# Revit family: Shower-Shower_Door-KOHLER-Prim-K-706533.rfa_
name_source: partatom
category: Specialty Equipment
units: mm (PartAtom-declared; Revit-internal decimal feet)

## family parameters
Cut with Voids When Loaded = No
Host = Face
OmniClass Number = 23.31.17.17
OmniClass Title = Shower Enclosures
Part Type = Normal
Room Calculation Point = No
Round Connector Dimension = Use Diameter
Shared = No

## types (6) — shared parameters
ADA Compliant = No
Assembly Code = C1030200
Date Modified = 06/28/2023
Default Elevation = 4"
Height = 79 1/16"
Length = 5 9/16"
Manufacturer = Kohler Co.
Master Format 2014 = 10 28 19.16
Master Format 2014 Name = Shower Doors
Material = Premium Metal Construction
Product Documentation Link = https://www.us.kohler.com
Product Name = Prim
Product Page URL = http://www.us.kohler.com
URL = http://www.us.kohler.com
WaterSense Certified = No

## per-type parameters (varying)
| type | Description | Finish | Handle Finish | Model | Secondary Finish | Type |
| Frosted Glass, SHP-Bright Polished Silver | Frameless sliding shower door, 79-1/16 inch H x 54-5/8 - 59-5/8 inch W, with 5/16 inch thick Frosted glass | Kohler-Metal-SHP-Bright_Polished_Silver | Kohler-Metal-CP-Polished_Chrome | K-706533-8D3-SHP | KOHLER-Frosted_Glass | 1 |
| Frosted Glass, BNK-Anodized Brushed Nickel | Frameless sliding shower door, 79-1/16 inch H x 54-5/8 - 59-5/8 inch W, with 5/16 inch thick Frosted glass | Kohler-Metal-BNK-Anodized_Brushed_Nickel | Kohler-Metal-BN-Vibrant_Brushed_Nickel | K-706533-8D3-BNK | KOHLER-Frosted_Glass | 2 |
| Frosted Glass, ABZ-Anodized Dark Bronze | Frameless sliding shower door, 79-1/16 inch H x 54-5/8 - 59-5/8 inch W, with 5/16 inch thick Frosted glass | Kohler-Metal-ABZ-Anodized_Dark_Bronze | KOHLER-Metal-2BL-Black | K-706533-8D3-ABZ | KOHLER-Frosted_Glass | 3 |
| Crystal Clear Glass, SHP-Bright Polished Silver | Frameless sliding shower door, 79-1/16 inch H x 54-5/8 - 59-5/8 inch W, with 5/16 inch thick Clear glass | Kohler-Metal-SHP-Bright_Polished_Silver | Kohler-Metal-CP-Polished_Chrome | K-706533-8L-SHP | Kohler-Glass-L-Crystal_Clear | 4 |
| Crystal Clear Glass, BNK-Anodized Brushed Nickel | Frameless sliding shower door, 79-1/16 inch H x 54-5/8 - 59-5/8 inch W, with 5/16 inch thick Clear glass | Kohler-Metal-BNK-Anodized_Brushed_Nickel | Kohler-Metal-BN-Vibrant_Brushed_Nickel | K-706533-8L-BNK | Kohler-Glass-L-Crystal_Clear | 5 |
| Crystal Clear Glass, ABZ-Anodized Dark Bronze | Frameless sliding shower door, 79-1/16 inch H x 54-5/8 - 59-5/8 inch W, with 5/16 inch thick Clear glass | Kohler-Metal-ABZ-Anodized_Dark_Bronze | KOHLER-Metal-2BL-Black | K-706533-8L-ABZ | Kohler-Glass-L-Crystal_Clear | 6 |

## geometry (parser evidence)
native form markers: Sweep x5
no freeform markers — native parametric forms only
